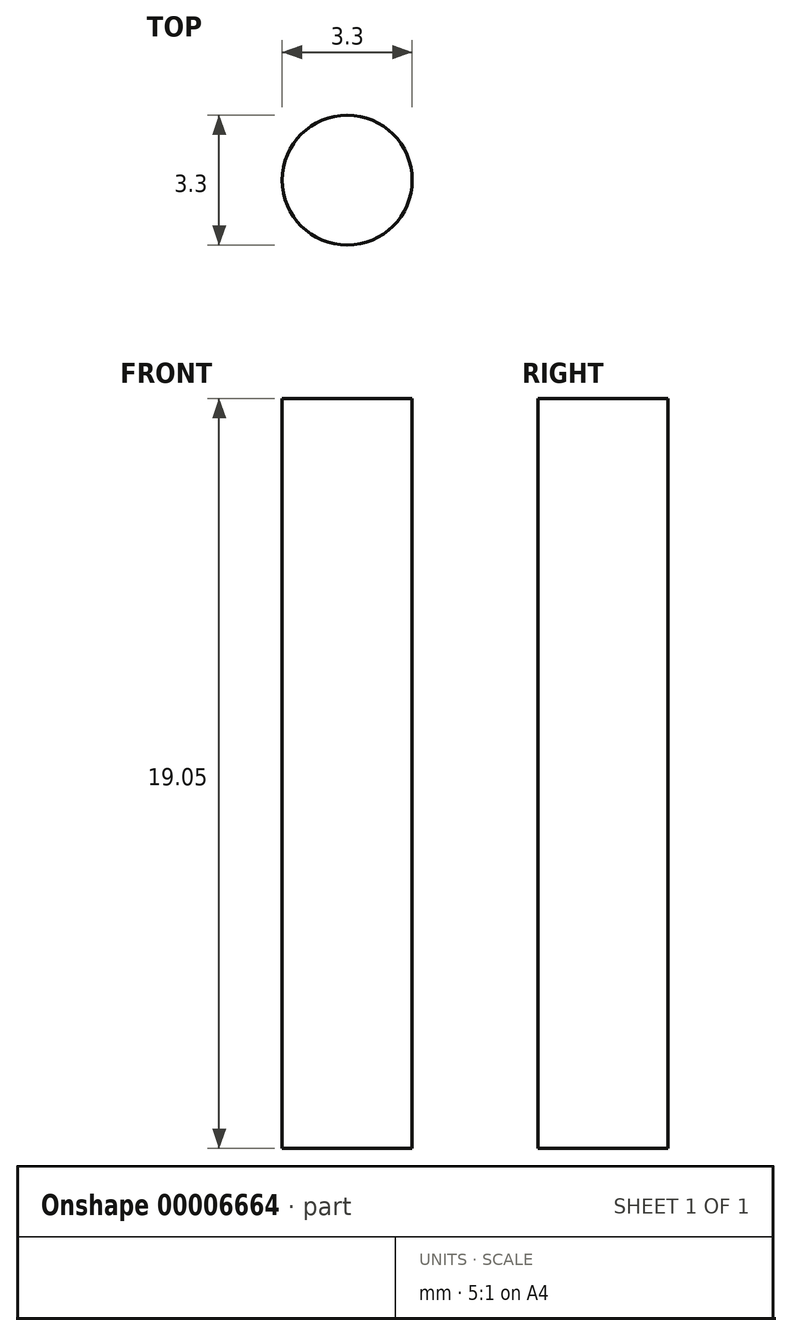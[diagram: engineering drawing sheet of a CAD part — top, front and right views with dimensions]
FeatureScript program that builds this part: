
annotation { "Feature Type Name" : "Feature", "Feature Type Description" : "" }
export const myFeature = defineFeature(function(context is Context, id is Id, definition is map)
    precondition{}
    {
        {
            var Q0;
            Q0=qCreatedBy(makeId("Top.planeOp"),FACE);
            var sketch = newSketch(context, id + "F0", { "sketchPlane" : qUnion([Q0])});
            skCircle(sketch, "E0", {"center": v(0, 0) * mm, "radius": 1.65 * mm});
            skSolve(sketch);
        }
        {
            var Q0;
            Q0 = qSketchRegion(id + "F0", true);
            extrude(context, id + "F1", {"entities" : qUnion([Q0]), "depth" : 19.05 * mm});
        }
    });
